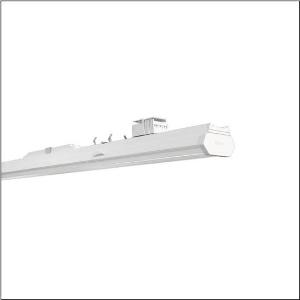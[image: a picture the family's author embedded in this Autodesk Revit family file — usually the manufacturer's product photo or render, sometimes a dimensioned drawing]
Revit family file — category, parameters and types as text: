
# Revit family: licross_r__21_protected_mo_52td1bvn45xgd_2e06
name_source: partatom
category: Lighting Fixtures
units: mm (PartAtom-declared; Revit-internal decimal feet)

## family parameters
Cut with Voids When Loaded = No
Host = Face
Light Source = No
Part Type = Normal
Room Calculation Point = No
Round Connector Dimension = Use Diameter
Shared = No

## types (1)
- --- (1 x LED, 5000 lm, 29.3 W, 4000K)
    Apparent Load = 29 VA
    CIE Flux Codes = 54 82 95 97 100
    Color Rendering = 80
    Color Temperature = 4000K
    Default Elevation = 1800 mm
    Description = Licross® 21 Protected MO, luminaire insert, of sheet steel, galvanised, coil coated, white, length: 1.500mm, width: 90mm, height: 101mm, LED rated luminous flux: 5.000lm, light colour: 840, control gear: DALI 2, CLO, control gear: ECG DALI, with plug, 6-pole, with phase selection, mains connection: 220..240V, AC/DC, 0/50..60Hz, start of lifetime: 29W, end of service life: 33W, halogen-free wiring, for central battery installations according to DIN EN 60598-2-22, for emergency light function, without changeover relay, primary optical cover: cover, of PMMA, light emission: direct distribution, primary light characteristic: symmetric, protection rating (complete): IP54, insulation class (complete): insulation class I (protective earthing), certification: CE, ENEC, VDE, UKCA, protection symbol: D if used in an environment with non-conductive dust loads with corresponding accessories, impact resistance: IK06, permissible ambient temperature for indoor applications: -25..+50°C, standard: EN 60598-2-22, corresponds to IFS (International Featured Standards) requirements for safety and quality in the food industry, reducing of maximum allowable ambient temperature of 5°C with ceiling mounting, LABS conformity tested according to VDMA 24364:2018-05, packaging unit: 1 piece
    Height = 92 mm
    Lamp = 1 x LED
    Lamp Light Flux = 5000 lm
    Lamp Power = 29.3 W
    Lamp count = 1
    Length = 1500 mm
    Luminous efficacy = 171 lm/W
    Manufacturer = Siteco
    ModVariant = No
    Model = 52TD1BVN45XGD
    Mounting Place = Ceiling
    Mounting Type = Pendant
    Number of Poles = 1
    OnlyDefault = Yes
    Power Factor = 1
    Product Name = Licross® 21 Protected MO
    Product group = luminaire insert
    ProductGroupID = 901
    Protection Class = Protection class I
    Protection Degree = IP 54
    RLX_Detail_Level = 1
    RLX_Emergency_Light_Flux = 0 lm
    RLX_Emergency_Type = 0
    RLX_Emergency_Type_DB = No
    RlxData = <blob elided: 24245 chars, md5=0f825079>
    Socket = socket
    Standby Power = 0 W
    System Light Flux = 5000 lm
    System Power = 29 W
    Type Comments = : AC-mode, luminous flux: 100 % | dim-lin: 254 | 199 mA
    Type Image = l_1256148.jpg
    URL = http://relux.com
    VarID = @adj_032445
    Voltage = 0 V
    Weight = 0.00 kg
    Width = 88 mm

## geometry (parser evidence)
native form markers: Blend x4, Sweep x10
no freeform markers — native parametric forms only
